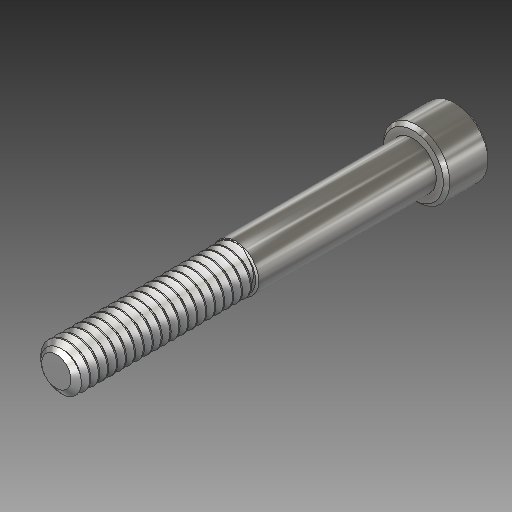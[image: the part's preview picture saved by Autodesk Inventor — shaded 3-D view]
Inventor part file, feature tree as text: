
AUTODESK INVENTOR PART (.ipt)
format: ipt  version: 2019.4 (Build 234330000, 330)  size: 679,424 bytes
history: native  units: in
note: dims shown in document units (in); Inventor stores cm internally (conversion verified against a paired STEP export)
features: chamfer x1
ambient origin geometry x8: Origin, YZ Plane, XZ Plane, XY Plane, X Axis, Y Axis, Z Axis, Center Point
bodies: Solid1 (feature_tree)
feature tree (1):
  chamfer  "Chamfer1"  [1 undecoded]
note: 1 required parameter value undecoded (feature->parameter linkage not recoverable at this tier; creation-order binding heuristic only, values carry confidence <= 0.55)
